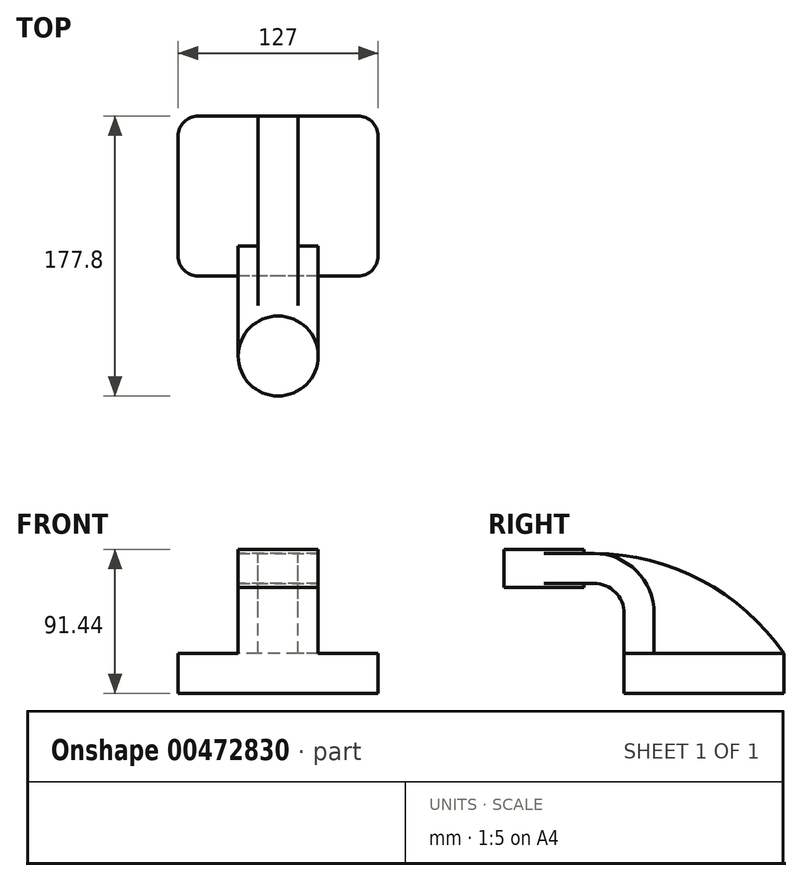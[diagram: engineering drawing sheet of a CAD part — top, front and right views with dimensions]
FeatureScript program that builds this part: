
annotation { "Feature Type Name" : "Feature", "Feature Type Description" : "" }
export const myFeature = defineFeature(function(context is Context, id is Id, definition is map)
    precondition{}
    {
        {
            var Q0;
            Q0=qCreatedBy(makeId("Right.planeOp"),FACE);
            var sketch = newSketch(context, id + "F0", { "sketchPlane" : qUnion([Q0])});
            skLineSegment(sketch, "E0.bottom", {"start": v(-50.8, -12.7) * mm, "end": v(50.8, -12.7) * mm});
            skLineSegment(sketch, "E0.top", {"start": v(-50.8, 12.7) * mm, "end": v(50.8, 12.7) * mm});
            skLineSegment(sketch, "E0.left", {"start": v(-50.8, -12.7) * mm, "end": v(-50.8, 12.7) * mm});
            skLineSegment(sketch, "E0.right", {"start": v(50.8, -12.7) * mm, "end": v(50.8, 12.7) * mm});
            skPoint(sketch, "E0.middle", {"position": v(0, 0) * mm});
            skLineSegment(sketch, "E1", {"start": v(-50.8, 12.7) * mm, "end": v(-50.8, 38.1) * mm});
            skArc(sketch, "E2", {"start": v(-50.8, 38.1) * mm, "mid": v(-56.38, 51.57) * mm, "end": v(-69.85, 57.15) * mm});
            skLineSegment(sketch, "E3", {"start": v(-69.85, 57.15) * mm, "end": v(-101.6, 57.15) * mm});
            skLineSegment(sketch, "E4.0", {"start": v(-69.85, 76.2) * mm, "end": v(-101.6, 76.2) * mm});
            skArc(sketch, "E4.1", {"start": v(-31.75, 38.1) * mm, "mid": v(-42.9, 65.04) * mm, "end": v(-69.85, 76.2) * mm});
            skLineSegment(sketch, "E4.2", {"start": v(-31.75, 12.7) * mm, "end": v(-31.75, 38.1) * mm});
            skLineSegment(sketch, "E5", {"start": v(-101.6, 76.2) * mm, "end": v(-101.6, 57.15) * mm});
            skSolve(sketch);
        }
        {
            var Q0;
            {var subQ0=sQuery(id+"F0.wireOp",EDGE,"E1");Q0=makeQuery(id+"F0.imprint","IMPRINT",FACE,{"disambiguationData":[TD([[makeQuery(id+"F0.imprint","IMPRINT",EDGE,{"derivedFrom":subQ0}),-1.0]])]});}
            extrude(context, id + "F1", {"entities" : qUnion([Q0]), "depth" : 25.4 * mm, "hasSecondDirection" : true, "secondDirectionOppositeDirection" : true, "secondDirectionDepth" : 25.4 * mm});
        }
        {
            var Q0;
            Q0=makeQuery(id+"F0.imprint","IMPRINT",FACE,{"disambiguationData":[TD([[makeQuery(id+"F0.imprint","IMPRINT",EDGE,{"derivedFrom":sQuery(id+"F0.wireOp",EDGE,"E0.bottom")}),1.0]])]});
            extrude(context, id + "F2", {"entities" : qUnion([Q0]), "operationType" : NewBodyOperationType.ADD, "depth" : 63.5 * mm, "hasSecondDirection" : true, "secondDirectionOppositeDirection" : true, "secondDirectionDepth" : 63.5 * mm});
        }
        {
            var Q0;
            Q0=makeQuery(id+"F1.opExtrude","SWEPT_FACE",FACE,{"disambiguationData":[OSD([sQuery(id+"F0.wireOp",EDGE,"E4.0")])]});
            var sketch = newSketch(context, id + "F3", { "sketchPlane" : qUnion([Q0])});
            skCircle(sketch, "E6", {"center": v(0, -101.6) * mm, "radius": 25.4 * mm});
            skSolve(sketch);
        }
        {
            var Q0;
            {var subQ1=sQuery(id+"F0.wireOp",EDGE,"E4.0");var subQ2=makeQuery(id+"F1.opExtrude","SWEPT_EDGE",EDGE,{"disambiguationData":[OSD([subQ1,sQuery(id+"F0.wireOp",EDGE,"E5")])]});Q0=makeQuery(id+"F3.imprint","IMPRINT",FACE,{"disambiguationData":[TD([[makeQuery(id+"F3.imprint","IMPRINT",EDGE,{"derivedFrom":subQ2}),-1.0]])]});}
            var Q1;
            {var subQ1=sQuery(id+"F0.wireOp",EDGE,"E4.0");var subQ2=makeQuery(id+"F1.opExtrude","SWEPT_EDGE",EDGE,{"disambiguationData":[OSD([subQ1,sQuery(id+"F0.wireOp",EDGE,"E5")])]});Q1=makeQuery(id+"F3.imprint","IMPRINT",FACE,{"disambiguationData":[TD([[makeQuery(id+"F3.imprint","IMPRINT",EDGE,{"derivedFrom":subQ2}),1.0]])]});}
            extrude(context, id + "F4", {"entities" : qUnion([Q0, Q1]), "operationType" : NewBodyOperationType.ADD, "depth" : 2.54 * mm, "hasSecondDirection" : true, "secondDirectionOppositeDirection" : true, "secondDirectionDepth" : 21.59 * mm});
        }
        {
            var Q0;
            Q0=qCreatedBy(makeId("Right.planeOp"),FACE);
            var sketch = newSketch(context, id + "F5", { "sketchPlane" : qUnion([Q0])});
            skPoint(sketch, "E7.0", {"position": v(-69.85, 76.2) * mm});
            skPoint(sketch, "E8.0", {"position": v(50.8, 12.7) * mm});
            skArc(sketch, "E9", {"start": v(50.8, 12.7) * mm, "mid": v(-1.75, 59.22) * mm, "end": v(-69.85, 76.2) * mm});
            skLineSegment(sketch, "E10.0", {"start": v(-31.75, 12.7) * mm, "end": v(50.8, 12.7) * mm});
            skLineSegment(sketch, "E11.0", {"start": v(-31.75, 12.7) * mm, "end": v(-31.75, 38.1) * mm});
            skArc(sketch, "E12.0", {"start": v(-31.75, 38.1) * mm, "mid": v(-42.9, 65.04) * mm, "end": v(-69.85, 76.2) * mm});
            skPoint(sketch, "E13.orphan", {"position": v(-50.8, 12.7) * mm});
            skSolve(sketch);
        }
        {
            var Q0;
            {var subQ0=sQuery(id+"F5.wireOp",EDGE,"E10.0");Q0=makeQuery(id+"F5.imprint","IMPRINT",FACE,{"disambiguationData":[TD([[makeQuery(id+"F5.imprint","IMPRINT",EDGE,{"derivedFrom":subQ0}),1.0]])]});}
            extrude(context, id + "F6", {"entities" : qUnion([Q0]), "operationType" : NewBodyOperationType.ADD, "depth" : 12.7 * mm, "hasSecondDirection" : true, "secondDirectionOppositeDirection" : true, "secondDirectionDepth" : 12.7 * mm});
        }
        {
            var Q0;
            Q0=makeQuery(id+"F2.opExtrude","CAP_EDGE",EDGE,{"disambiguationData":[OSD([sQuery(id+"F0.wireOp",EDGE,"E0.right")])],"isStart":true});
            var Q1;
            Q1=makeQuery(id+"F2.opExtrude","CAP_EDGE",EDGE,{"disambiguationData":[OSD([sQuery(id+"F0.wireOp",EDGE,"E0.left")])],"isStart":true});
            var Q2;
            Q2=makeQuery(id+"F2.opExtrude","CAP_EDGE",EDGE,{"disambiguationData":[OSD([sQuery(id+"F0.wireOp",EDGE,"E0.left")])],"isStart":false});
            var Q3;
            Q3=makeQuery(id+"F2.opExtrude","CAP_EDGE",EDGE,{"disambiguationData":[OSD([sQuery(id+"F0.wireOp",EDGE,"E0.right")])],"isStart":false});
            fillet(context, id + "F7", {"entities" : qUnion([Q0, Q1, Q2, Q3]), "radius" : 12.7 * mm, "tangentPropagation" : true, "allowEdgeOverflow" : false});
        }
    });
